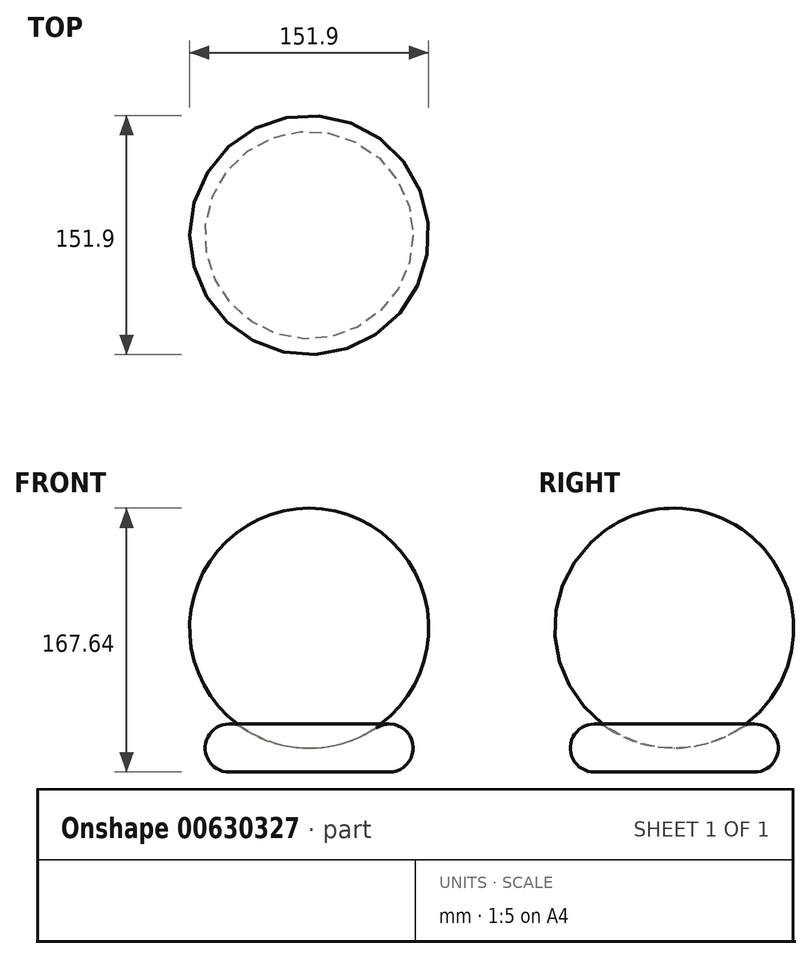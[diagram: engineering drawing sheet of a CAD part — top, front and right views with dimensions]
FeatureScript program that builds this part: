
annotation { "Feature Type Name" : "Feature", "Feature Type Description" : "" }
export const myFeature = defineFeature(function(context is Context, id is Id, definition is map)
    precondition{}
    {
        {
            var Q0;
            Q0=qCreatedBy(makeId("Front.planeOp"),FACE);
            var sketch = newSketch(context, id + "F0", { "sketchPlane" : qUnion([Q0])});
            skArc(sketch, "E0", {"start": v(-42.38, 27.94) * mm, "mid": v(-65.4, 19.64) * mm, "end": v(-50.8, 0) * mm});
            skArc(sketch, "E1", {"start": v(-42.38, 27.94) * mm, "mid": v(-22.13, 18.45) * mm, "end": v(0, 15.24) * mm});
            skLineSegment(sketch, "E2", {"start": v(0, 0) * mm, "end": v(-50.8, 0) * mm});
            skPoint(sketch, "E3.start.orphan", {"position": v(0, 3.95) * mm});
            skLineSegment(sketch, "E4", {"start": v(0, 15.24) * mm, "end": v(0, 0) * mm});
            skSolve(sketch);
        }
        {
            var Q0;
            Q0=makeQuery(id+"F0.imprint","IMPRINT",FACE,{"disambiguationData":[TD([[makeQuery(id+"F0.imprint","IMPRINT",EDGE,{"derivedFrom":sQuery(id+"F0.wireOp",EDGE,"E0")}),1.0]])]});
            var Q1;
            Q1=sQuery(id+"F0.wireOp",EDGE,"E4");
            revolve(context, id + "F1", {"entities" : qUnion([Q0]), "axis" : qUnion([Q1]), "revolveType" : RevolveType.FULL});
        }
        {
            var Q0;
            Q0=qCreatedBy(makeId("Top.planeOp"),FACE);
            cPlane(context, id + "F2", {"entities" : qUnion([Q0]), "cplaneType" : CPlaneType.OFFSET, "offset" : 50.8 * mm, "width" : 152.4 * mm, "height" : 152.4 * mm});
        }
    });
